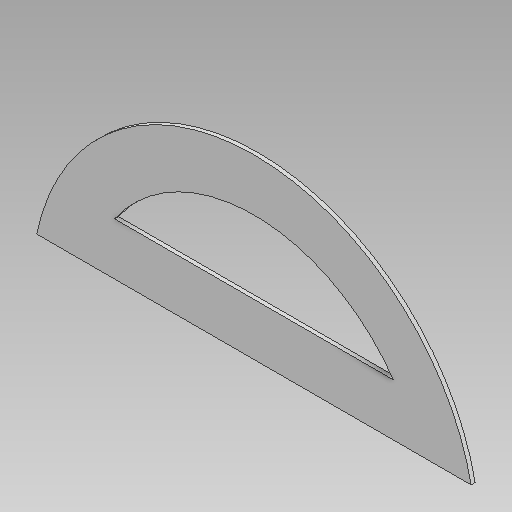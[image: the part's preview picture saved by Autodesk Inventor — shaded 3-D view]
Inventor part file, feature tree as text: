
AUTODESK INVENTOR PART (.ipt)
format: ipt  version: 2021 (Build 250183000, 183)  size: 112,128 bytes
history: native  units: mm
features: extrude x2, sketch x2, projected_geometry x1
ambient origin geometry x8: Origin, YZ Plane, XZ Plane, XY Plane, X Axis, Y Axis, Z Axis, Center Point
bodies: Body1 (feature_tree)
feature tree (5):
  extrude  "side"  TaperAngle=0.0deg  [1 undecoded]
  extrude  "Extrusion3"  Depth=1090.0mm
  sketch  "Sketch2"  dims[d14=20.0mm d15=0.0mm d17=0.0mm]
  sketch  "Sketch3"  dims[d21=0.0mm d24=890.0mm d25=2180.0mm d26=1090.0mm d28=1400.0mm d29=0.0mm d30=0.0mm]
  projected_geometry  "Projected Loop1"
note: 1 required parameter value undecoded (feature->parameter linkage not recoverable at this tier; creation-order binding heuristic only, values carry confidence <= 0.55)
